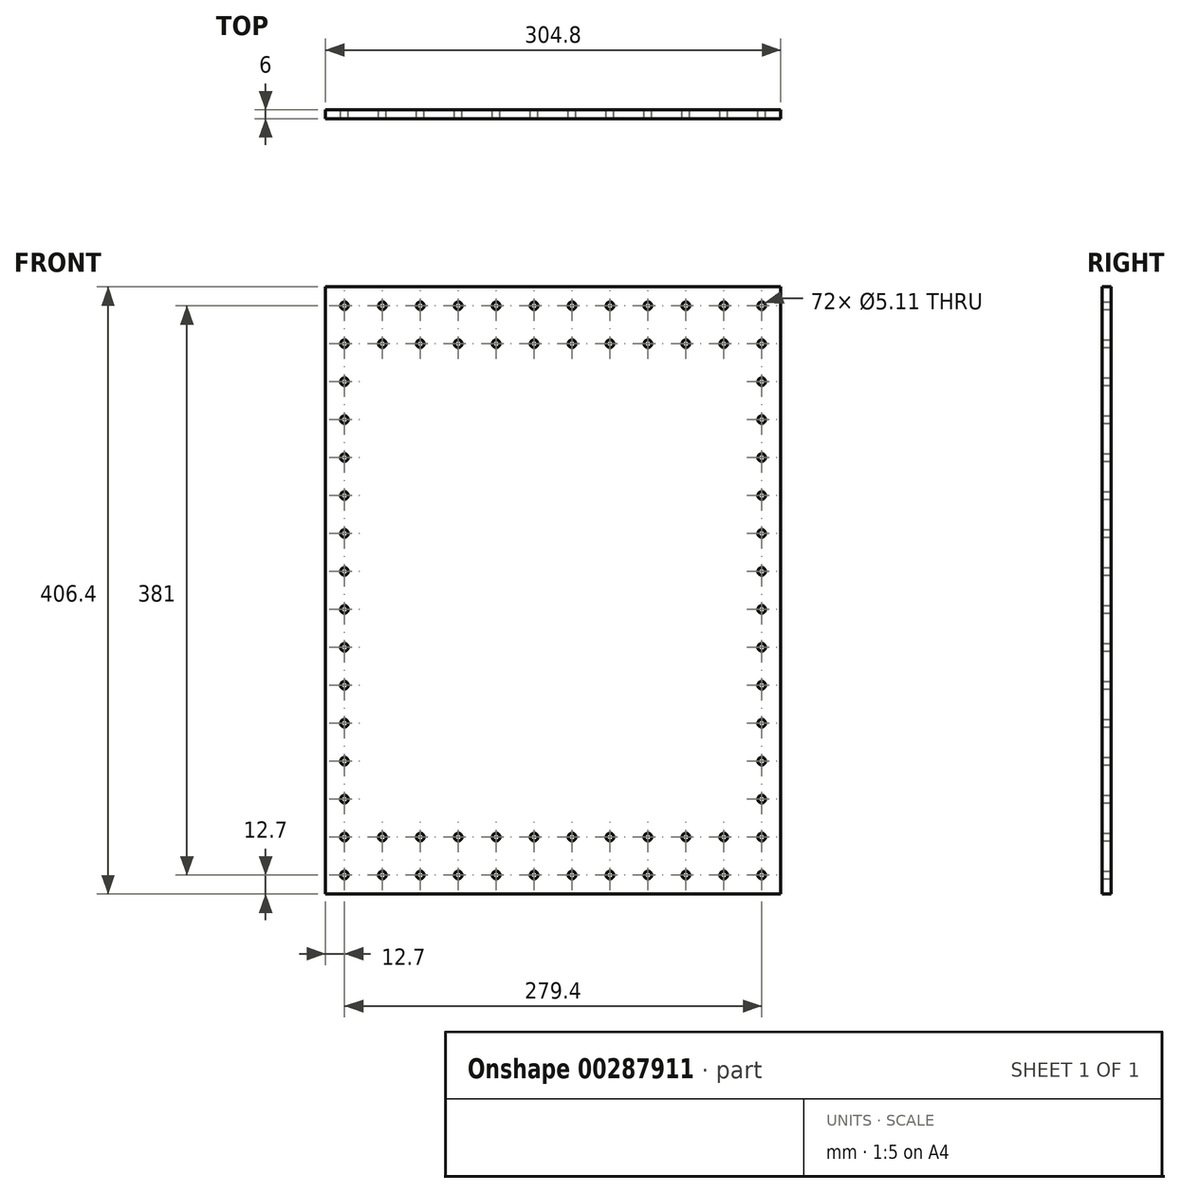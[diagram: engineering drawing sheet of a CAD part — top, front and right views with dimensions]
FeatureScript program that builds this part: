
annotation { "Feature Type Name" : "Feature", "Feature Type Description" : "" }
export const myFeature = defineFeature(function(context is Context, id is Id, definition is map)
    precondition{}
    {
        {
            var Q0;
            Q0=qCreatedBy(makeId("Front.planeOp"),FACE);
            var sketch = newSketch(context, id + "F0", { "sketchPlane" : qUnion([Q0])});
            skLineSegment(sketch, "E0.bottom", {"start": v(152.4, 203.2) * mm, "end": v(-152.4, 203.2) * mm});
            skLineSegment(sketch, "E0.top", {"start": v(152.4, -203.2) * mm, "end": v(-152.4, -203.2) * mm});
            skLineSegment(sketch, "E0.left", {"start": v(152.4, 203.2) * mm, "end": v(152.4, -203.2) * mm});
            skLineSegment(sketch, "E0.right", {"start": v(-152.4, 203.2) * mm, "end": v(-152.4, -203.2) * mm});
            skPoint(sketch, "E0.middle", {"position": v(0, 0) * mm});
            skCircle(sketch, "E1", {"center": v(-139.7, 190.5) * mm, "radius": 2.55 * mm});
            skCircle(sketch, "E2.0.1.0", {"center": v(-139.7, 165.1) * mm, "radius": 2.55 * mm});
            skCircle(sketch, "E2.0.2.0", {"center": v(-139.7, 139.7) * mm, "radius": 2.55 * mm});
            skCircle(sketch, "E2.0.3.0", {"center": v(-139.7, 114.3) * mm, "radius": 2.55 * mm});
            skCircle(sketch, "E2.0.4.0", {"center": v(-139.7, 88.9) * mm, "radius": 2.55 * mm});
            skCircle(sketch, "E2.0.5.0", {"center": v(-139.7, 63.5) * mm, "radius": 2.55 * mm});
            skCircle(sketch, "E2.0.6.0", {"center": v(-139.7, 38.1) * mm, "radius": 2.55 * mm});
            skCircle(sketch, "E2.0.7.0", {"center": v(-139.7, 12.7) * mm, "radius": 2.55 * mm});
            skCircle(sketch, "E2.0.8.0", {"center": v(-139.7, -12.7) * mm, "radius": 2.55 * mm});
            skCircle(sketch, "E2.0.9.0", {"center": v(-139.7, -38.1) * mm, "radius": 2.55 * mm});
            skCircle(sketch, "E2.0.10.0", {"center": v(-139.7, -63.5) * mm, "radius": 2.55 * mm});
            skCircle(sketch, "E2.0.11.0", {"center": v(-139.7, -88.9) * mm, "radius": 2.55 * mm});
            skCircle(sketch, "E2.0.12.0", {"center": v(-139.7, -114.3) * mm, "radius": 2.55 * mm});
            skCircle(sketch, "E2.0.13.0", {"center": v(-139.7, -139.7) * mm, "radius": 2.55 * mm});
            skCircle(sketch, "E2.0.14.0", {"center": v(-139.7, -165.1) * mm, "radius": 2.55 * mm});
            skCircle(sketch, "E2.0.15.0", {"center": v(-139.7, -190.5) * mm, "radius": 2.55 * mm});
            skCircle(sketch, "E2.1.0.0", {"center": v(139.7, 190.5) * mm, "radius": 2.55 * mm});
            skCircle(sketch, "E2.1.1.0", {"center": v(139.7, 165.1) * mm, "radius": 2.55 * mm});
            skCircle(sketch, "E2.1.2.0", {"center": v(139.7, 139.7) * mm, "radius": 2.55 * mm});
            skCircle(sketch, "E2.1.3.0", {"center": v(139.7, 114.3) * mm, "radius": 2.55 * mm});
            skCircle(sketch, "E2.1.4.0", {"center": v(139.7, 88.9) * mm, "radius": 2.55 * mm});
            skCircle(sketch, "E2.1.5.0", {"center": v(139.7, 63.5) * mm, "radius": 2.55 * mm});
            skCircle(sketch, "E2.1.6.0", {"center": v(139.7, 38.1) * mm, "radius": 2.55 * mm});
            skCircle(sketch, "E2.1.7.0", {"center": v(139.7, 12.7) * mm, "radius": 2.55 * mm});
            skCircle(sketch, "E2.1.8.0", {"center": v(139.7, -12.7) * mm, "radius": 2.55 * mm});
            skCircle(sketch, "E2.1.9.0", {"center": v(139.7, -38.1) * mm, "radius": 2.55 * mm});
            skCircle(sketch, "E2.1.10.0", {"center": v(139.7, -63.5) * mm, "radius": 2.55 * mm});
            skCircle(sketch, "E2.1.11.0", {"center": v(139.7, -88.9) * mm, "radius": 2.55 * mm});
            skCircle(sketch, "E2.1.12.0", {"center": v(139.7, -114.3) * mm, "radius": 2.55 * mm});
            skCircle(sketch, "E2.1.13.0", {"center": v(139.7, -139.7) * mm, "radius": 2.55 * mm});
            skCircle(sketch, "E2.1.14.0", {"center": v(139.7, -165.1) * mm, "radius": 2.55 * mm});
            skCircle(sketch, "E2.1.15.0", {"center": v(139.7, -190.5) * mm, "radius": 2.55 * mm});
            skLineSegment(sketch, "E2.direction1", {"start": v(-139.7, 190.5) * mm, "end": v(139.7, 190.5) * mm, "construction": true});
            skLineSegment(sketch, "E2.direction2", {"start": v(-139.7, 190.5) * mm, "end": v(-139.7, 165.1) * mm, "construction": true});
            skCircle(sketch, "E3.1.0.0", {"center": v(-114.3, 190.5) * mm, "radius": 2.55 * mm});
            skCircle(sketch, "E3.1.1.0", {"center": v(-114.3, 165.1) * mm, "radius": 2.55 * mm});
            skCircle(sketch, "E3.2.0.0", {"center": v(-88.9, 190.5) * mm, "radius": 2.55 * mm});
            skCircle(sketch, "E3.2.1.0", {"center": v(-88.9, 165.1) * mm, "radius": 2.55 * mm});
            skCircle(sketch, "E3.3.0.0", {"center": v(-63.5, 190.5) * mm, "radius": 2.55 * mm});
            skCircle(sketch, "E3.3.1.0", {"center": v(-63.5, 165.1) * mm, "radius": 2.55 * mm});
            skCircle(sketch, "E3.4.0.0", {"center": v(-38.1, 190.5) * mm, "radius": 2.55 * mm});
            skCircle(sketch, "E3.4.1.0", {"center": v(-38.1, 165.1) * mm, "radius": 2.55 * mm});
            skCircle(sketch, "E3.5.0.0", {"center": v(-12.7, 190.5) * mm, "radius": 2.55 * mm});
            skCircle(sketch, "E3.5.1.0", {"center": v(-12.7, 165.1) * mm, "radius": 2.55 * mm});
            skCircle(sketch, "E3.6.0.0", {"center": v(12.7, 190.5) * mm, "radius": 2.55 * mm});
            skCircle(sketch, "E3.6.1.0", {"center": v(12.7, 165.1) * mm, "radius": 2.55 * mm});
            skCircle(sketch, "E3.7.0.0", {"center": v(38.1, 190.5) * mm, "radius": 2.55 * mm});
            skCircle(sketch, "E3.7.1.0", {"center": v(38.1, 165.1) * mm, "radius": 2.55 * mm});
            skCircle(sketch, "E3.8.0.0", {"center": v(63.5, 190.5) * mm, "radius": 2.55 * mm});
            skCircle(sketch, "E3.8.1.0", {"center": v(63.5, 165.1) * mm, "radius": 2.55 * mm});
            skCircle(sketch, "E3.9.0.0", {"center": v(88.9, 190.5) * mm, "radius": 2.55 * mm});
            skCircle(sketch, "E3.9.1.0", {"center": v(88.9, 165.1) * mm, "radius": 2.55 * mm});
            skCircle(sketch, "E3.10.0.0", {"center": v(114.3, 190.5) * mm, "radius": 2.55 * mm});
            skCircle(sketch, "E3.10.1.0", {"center": v(114.3, 165.1) * mm, "radius": 2.55 * mm});
            skLineSegment(sketch, "E3.direction1", {"start": v(-139.7, 190.5) * mm, "end": v(-114.3, 190.5) * mm, "construction": true});
            skCircle(sketch, "E4.1.0.0", {"center": v(-114.3, -190.5) * mm, "radius": 2.55 * mm});
            skCircle(sketch, "E4.1.1.0", {"center": v(-114.3, -165.1) * mm, "radius": 2.55 * mm});
            skCircle(sketch, "E4.2.0.0", {"center": v(-88.9, -190.5) * mm, "radius": 2.55 * mm});
            skCircle(sketch, "E4.2.1.0", {"center": v(-88.9, -165.1) * mm, "radius": 2.55 * mm});
            skCircle(sketch, "E4.3.0.0", {"center": v(-63.5, -190.5) * mm, "radius": 2.55 * mm});
            skCircle(sketch, "E4.3.1.0", {"center": v(-63.5, -165.1) * mm, "radius": 2.55 * mm});
            skCircle(sketch, "E4.4.0.0", {"center": v(-38.1, -190.5) * mm, "radius": 2.55 * mm});
            skCircle(sketch, "E4.4.1.0", {"center": v(-38.1, -165.1) * mm, "radius": 2.55 * mm});
            skCircle(sketch, "E4.5.0.0", {"center": v(-12.7, -190.5) * mm, "radius": 2.55 * mm});
            skCircle(sketch, "E4.5.1.0", {"center": v(-12.7, -165.1) * mm, "radius": 2.55 * mm});
            skCircle(sketch, "E4.6.0.0", {"center": v(12.7, -190.5) * mm, "radius": 2.55 * mm});
            skCircle(sketch, "E4.6.1.0", {"center": v(12.7, -165.1) * mm, "radius": 2.55 * mm});
            skCircle(sketch, "E4.7.0.0", {"center": v(38.1, -190.5) * mm, "radius": 2.55 * mm});
            skCircle(sketch, "E4.7.1.0", {"center": v(38.1, -165.1) * mm, "radius": 2.55 * mm});
            skCircle(sketch, "E4.8.0.0", {"center": v(63.5, -190.5) * mm, "radius": 2.55 * mm});
            skCircle(sketch, "E4.8.1.0", {"center": v(63.5, -165.1) * mm, "radius": 2.55 * mm});
            skCircle(sketch, "E4.9.0.0", {"center": v(88.9, -190.5) * mm, "radius": 2.55 * mm});
            skCircle(sketch, "E4.9.1.0", {"center": v(88.9, -165.1) * mm, "radius": 2.55 * mm});
            skCircle(sketch, "E4.10.0.0", {"center": v(114.3, -190.5) * mm, "radius": 2.55 * mm});
            skCircle(sketch, "E4.10.1.0", {"center": v(114.3, -165.1) * mm, "radius": 2.55 * mm});
            skLineSegment(sketch, "E4.direction1", {"start": v(-139.7, -190.5) * mm, "end": v(-114.3, -190.5) * mm, "construction": true});
            skLineSegment(sketch, "E4.direction2", {"start": v(-139.7, -190.5) * mm, "end": v(-139.7, -165.1) * mm, "construction": true});
            skSolve(sketch);
        }
        {
            var Q0;
            Q0=makeQuery(id+"F0.imprint","IMPRINT",FACE,{"disambiguationData":[TD([[makeQuery(id+"F0.imprint","IMPRINT",EDGE,{"derivedFrom":sQuery(id+"F0.wireOp",EDGE,"E0.bottom")}),1.0]])]});
            extrude(context, id + "F1", {"entities" : qUnion([Q0]), "depth" : 6 * mm});
        }
    });
